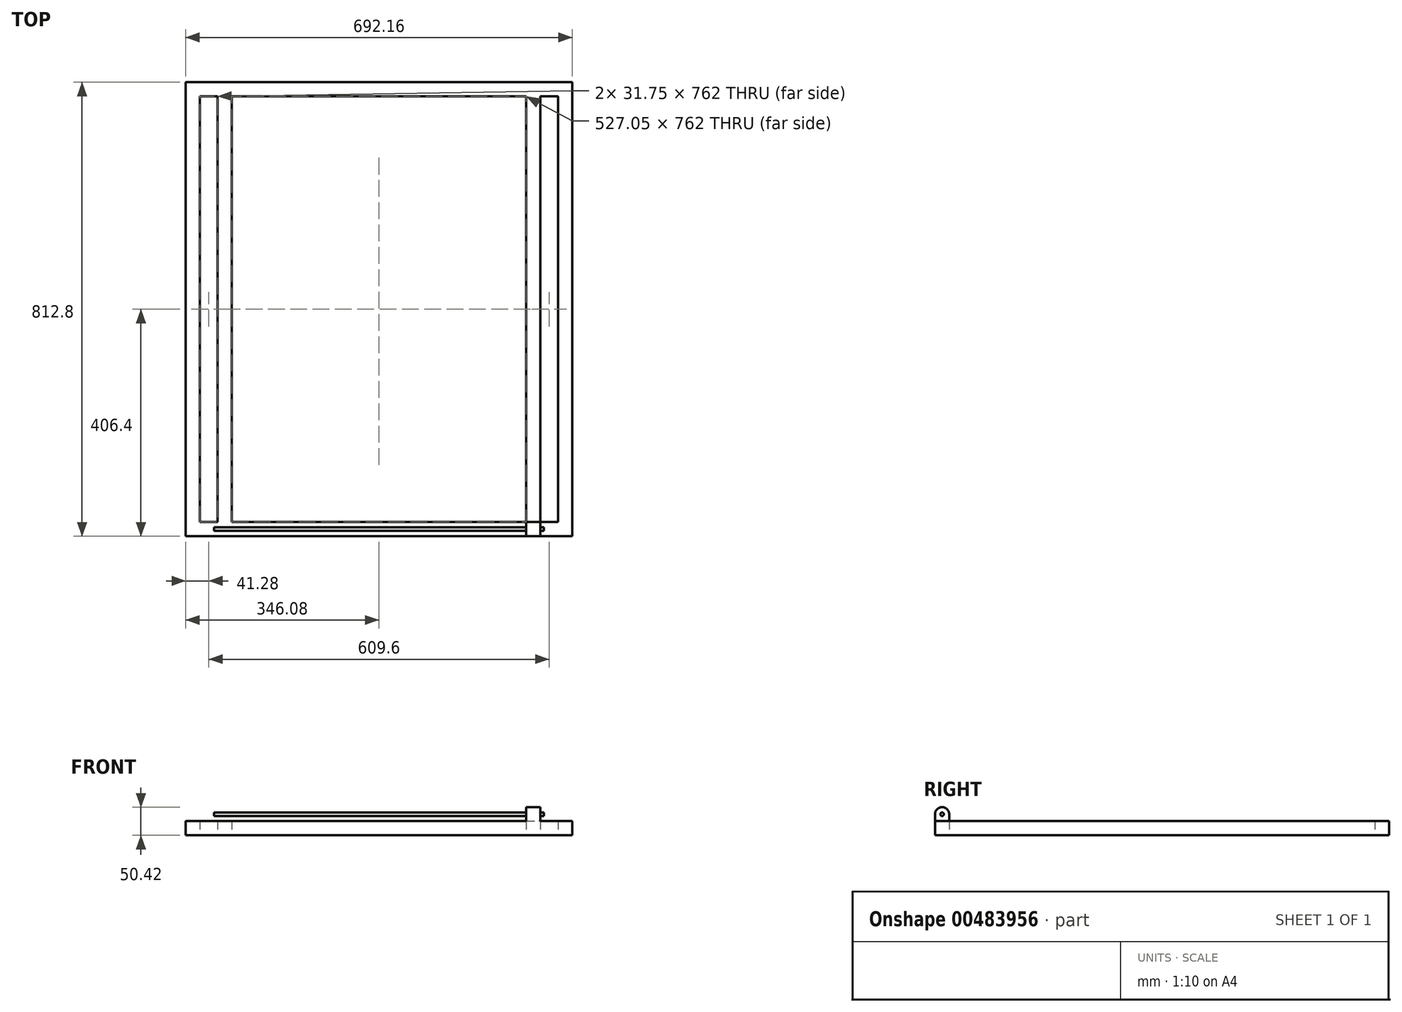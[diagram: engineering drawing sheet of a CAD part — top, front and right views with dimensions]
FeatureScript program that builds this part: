
annotation { "Feature Type Name" : "Feature", "Feature Type Description" : "" }
export const myFeature = defineFeature(function(context is Context, id is Id, definition is map)
    precondition{}
    {
        {
            var Q0;
            Q0=qCreatedBy(makeId("Top.planeOp"),FACE);
            var sketch = newSketch(context, id + "F0", { "sketchPlane" : qUnion([Q0])});
            skLineSegment(sketch, "E0.bottom", {"start": v(320.68, -12.7) * mm, "end": v(288.93, -12.7) * mm});
            skLineSegment(sketch, "E0.top", {"start": v(346.07, 12.7) * mm, "end": v(-346.08, 12.7) * mm});
            skLineSegment(sketch, "E0.left", {"start": v(346.07, -12.7) * mm, "end": v(346.07, 12.7) * mm});
            skPoint(sketch, "E0.middle", {"position": v(0, 0) * mm});
            skLineSegment(sketch, "E1", {"start": v(-346.08, 12.7) * mm, "end": v(-346.07, -800.1) * mm});
            skLineSegment(sketch, "E2", {"start": v(-320.68, -12.7) * mm, "end": v(-320.68, -774.7) * mm});
            skLineSegment(sketch, "E3", {"start": v(-346.07, -800.1) * mm, "end": v(346.08, -800.1) * mm});
            skLineSegment(sketch, "E4", {"start": v(346.08, -800.1) * mm, "end": v(346.07, 12.7) * mm});
            skLineSegment(sketch, "E5", {"start": v(320.68, -12.7) * mm, "end": v(320.68, -774.7) * mm});
            skLineSegment(sketch, "E6", {"start": v(-320.68, -774.7) * mm, "end": v(-288.92, -774.7) * mm});
            skLineSegment(sketch, "E7", {"start": v(-263.52, -774.7) * mm, "end": v(-263.53, -12.7) * mm});
            skLineSegment(sketch, "E8", {"start": v(-288.93, -12.7) * mm, "end": v(-288.92, -774.7) * mm});
            skLineSegment(sketch, "E9.trimOffspring", {"start": v(-263.52, -774.7) * mm, "end": v(263.52, -774.7) * mm});
            skLineSegment(sketch, "E10.trimOffspring", {"start": v(-288.93, -12.7) * mm, "end": v(-320.68, -12.7) * mm});
            skLineSegment(sketch, "E11.MirrorCS", {"start": v(288.93, -12.7) * mm, "end": v(320.68, -12.7) * mm});
            skLineSegment(sketch, "E12.MirrorCS", {"start": v(320.68, -774.7) * mm, "end": v(288.92, -774.7) * mm});
            skLineSegment(sketch, "E13.MirrorCS", {"start": v(263.53, -774.7) * mm, "end": v(263.52, -12.7) * mm});
            skLineSegment(sketch, "E14.MirrorCS", {"start": v(288.92, -12.7) * mm, "end": v(288.92, -774.7) * mm});
            skLineSegment(sketch, "E15.trimOffspring", {"start": v(263.53, -12.7) * mm, "end": v(-263.53, -12.7) * mm});
            skLineSegment(sketch, "E16.trimOffspring", {"start": v(288.92, -774.7) * mm, "end": v(320.68, -774.7) * mm});
            skSolve(sketch);
        }
        {
            var Q0;
            Q0 = qSketchRegion(id + "F0", true);
            extrude(context, id + "F1", {"entities" : qUnion([Q0]), "endBound" : BoundingType.SYMMETRIC, "depth" : 25.4 * mm});
        }
        {
            var Q0;
            Q0=makeQuery(id+"F1.opExtrude","SWEPT_FACE",FACE,{"disambiguationData":[OSD([sQuery(id+"F0.wireOp",EDGE,"E13.MirrorCS")])]});
            var sketch = newSketch(context, id + "F2", { "sketchPlane" : qUnion([Q0])});
            skLineSegment(sketch, "E17", {"start": v(800.1, 12.7) * mm, "end": v(800.1, -12.7) * mm});
            skLineSegment(sketch, "E18", {"start": v(800.1, -12.7) * mm, "end": v(774.7, -12.7) * mm});
            skLineSegment(sketch, "E19", {"start": v(774.7, -12.7) * mm, "end": v(774.7, 12.7) * mm});
            skLineSegment(sketch, "E20", {"start": v(800.1, 25.02) * mm, "end": v(800.1, 12.7) * mm});
            skLineSegment(sketch, "E21", {"start": v(774.7, 12.7) * mm, "end": v(774.7, 25.02) * mm});
            skArc(sketch, "E22", {"start": v(800.1, 25.02) * mm, "mid": v(787.4, 37.72) * mm, "end": v(774.7, 25.02) * mm});
            skCircle(sketch, "E23", {"center": v(787.4, 25.02) * mm, "radius": 3.18 * mm});
            skSolve(sketch);
        }
        {
            var Q0;
            Q0=makeQuery(id+"F2.imprint","IMPRINT",FACE,{"disambiguationData":[TD([[makeQuery(id+"F2.imprint","IMPRINT",EDGE,{"derivedFrom":sQuery(id+"F2.wireOp",EDGE,"E17")}),-1.0]])]});
            extrude(context, id + "F3", {"entities" : qUnion([Q0]), "operationType" : NewBodyOperationType.ADD, "oppositeDirection" : true, "depth" : 25.4 * mm, "offsetDistance" : 25.4 * mm});
        }
        {
            var Q0;
            Q0=makeQuery(id+"F2.imprint","IMPRINT",FACE,{"disambiguationData":[TD([[makeQuery(id+"F2.imprint","IMPRINT",EDGE,{"derivedFrom":sQuery(id+"F2.wireOp",EDGE,"E23")}),1.0]])]});
            extrude(context, id + "F4", {"entities" : qUnion([Q0]), "depth" : 558.8 * mm, "offsetDistance" : 25.4 * mm});
        }
        {
            var Q0;
            Q0=makeQuery(id+"F2.imprint","IMPRINT",FACE,{"disambiguationData":[TD([[makeQuery(id+"F2.imprint","IMPRINT",EDGE,{"derivedFrom":sQuery(id+"F2.wireOp",EDGE,"E23")}),1.0]])]});
            extrude(context, id + "F5", {"entities" : qUnion([Q0]), "operationType" : NewBodyOperationType.ADD, "oppositeDirection" : true, "depth" : 31.75 * mm, "offsetDistance" : 25.4 * mm});
        }
    });
